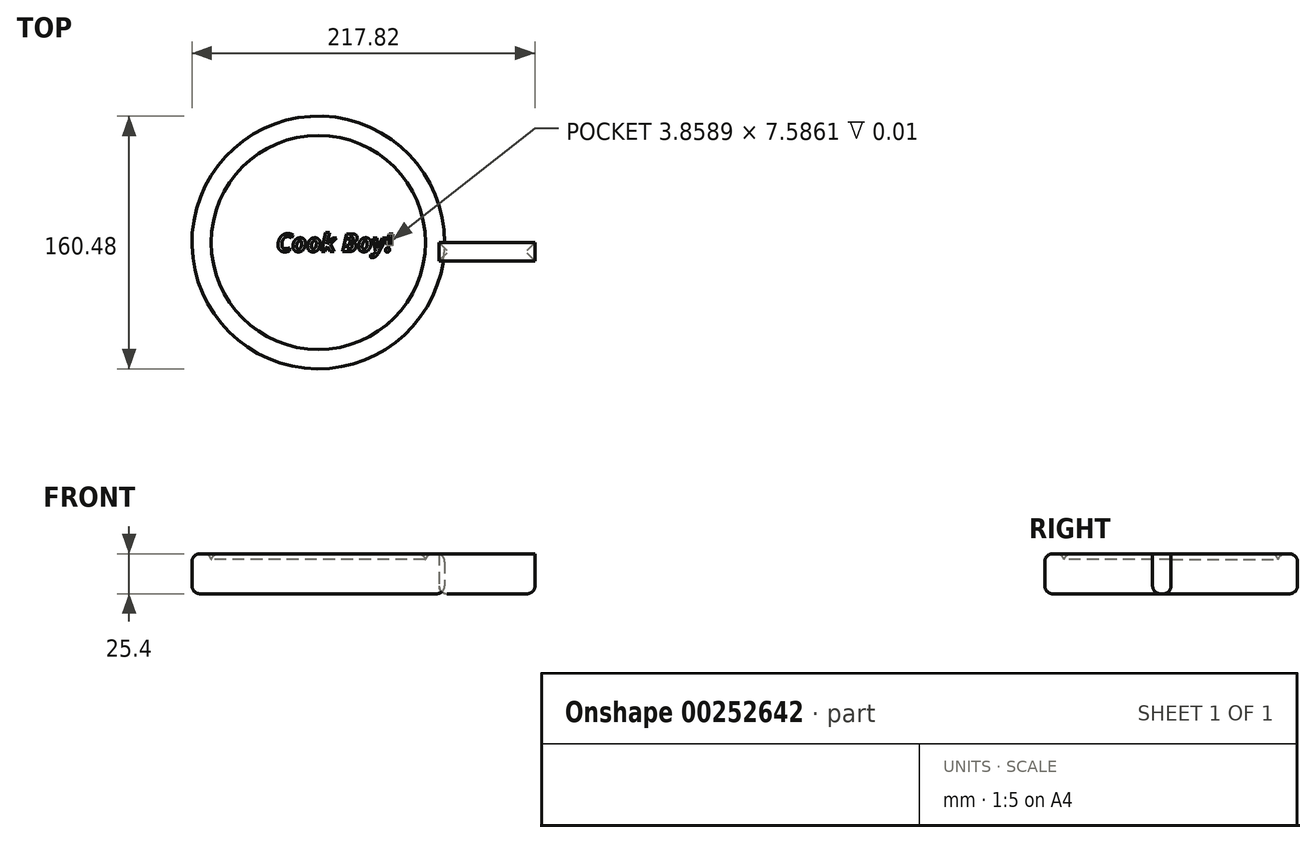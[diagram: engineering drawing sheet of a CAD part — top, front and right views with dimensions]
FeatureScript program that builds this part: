
annotation { "Feature Type Name" : "Feature", "Feature Type Description" : "" }
export const myFeature = defineFeature(function(context is Context, id is Id, definition is map)
    precondition{}
    {
        {
            var Q0;
            Q0=qCreatedBy(makeId("Top.planeOp"),FACE);
            var sketch = newSketch(context, id + "F0", { "sketchPlane" : qUnion([Q0])});
            skCircle(sketch, "E0", {"center": v(0, 0) * mm, "radius": 80.24 * mm});
            skSolve(sketch);
        }
        {
            var Q0;
            Q0=makeQuery(id+"F0.imprint","IMPRINT",FACE,{"disambiguationData":[TD([[makeQuery(id+"F0.imprint","IMPRINT",EDGE,{"derivedFrom":sQuery(id+"F0.wireOp",EDGE,"E0")}),1.0]])]});
            extrude(context, id + "F1", {"entities" : qUnion([Q0]), "depth" : 25.4 * mm});
        }
        {
            var Q0;
            Q0=makeQuery(id+"F1.opExtrude","CAP_FACE",FACE,{"disambiguationData":[OSD([sQuery(id+"F0.wireOp",EDGE,"E0")])],"isStart":false});
            var sketch = newSketch(context, id + "F2", { "sketchPlane" : qUnion([Q0])});
            skCircle(sketch, "E1", {"center": v(0, 0) * mm, "radius": 67.81 * mm});
            skSolve(sketch);
        }
        {
            var Q0;
            Q0=makeQuery(id+"F2.imprint","IMPRINT",FACE,{"disambiguationData":[TD([[makeQuery(id+"F2.imprint","IMPRINT",EDGE,{"derivedFrom":sQuery(id+"F2.wireOp",EDGE,"E1")}),1.0]])]});
            extrude(context, id + "F3", {"entities" : qUnion([Q0]), "operationType" : NewBodyOperationType.REMOVE, "oppositeDirection" : true, "depth" : 25.4 * mm});
        }
        {
            var Q0;
            Q0=makeQuery(id+"F1.opExtrude","CAP_FACE",FACE,{"disambiguationData":[OSD([sQuery(id+"F0.wireOp",EDGE,"E0")])],"isStart":false});
            fillet(context, id + "F4", {"entities" : qUnion([Q0]), "radius" : 5.08 * mm, "tangentPropagation" : true, "allowEdgeOverflow" : false});
        }
        {
            var Q0;
            Q0=qCreatedBy(makeId("Top.planeOp"),FACE);
            var sketch = newSketch(context, id + "F5", { "sketchPlane" : qUnion([Q0])});
            skCircle(sketch, "E2", {"center": v(0, 0) * mm, "radius": 68 * mm});
            skSolve(sketch);
        }
        {
            var Q0;
            Q0=makeQuery(id+"F5.imprint","IMPRINT",FACE,{"disambiguationData":[TD([[makeQuery(id+"F5.imprint","IMPRINT",EDGE,{"derivedFrom":sQuery(id+"F5.wireOp",EDGE,"E2")}),1.0]])]});
            extrude(context, id + "F6", {"entities" : qUnion([Q0]), "operationType" : NewBodyOperationType.ADD, "depth" : 25.4 * mm});
        }
        {
            var Q0;
            Q0=makeQuery(id+"F6.opExtrude","CAP_FACE",FACE,{"disambiguationData":[OSD([sQuery(id+"F5.wireOp",EDGE,"E2")])],"isStart":false});
            fillet(context, id + "F7", {"entities" : qUnion([Q0]), "radius" : 5.08 * mm, "tangentPropagation" : true, "allowEdgeOverflow" : false});
        }
        {
            var Q0;
            Q0=makeQuery(id+"F6.boolean.opBoolean","MERGE",FACE,{"derivedFrom":[makeQuery(id+"F1.opExtrude","CAP_FACE",FACE,{"disambiguationData":[OSD([sQuery(id+"F0.wireOp",EDGE,"E0")])],"isStart":true}),makeQuery(id+"F6.opExtrude","CAP_FACE",FACE,{"disambiguationData":[OSD([sQuery(id+"F5.wireOp",EDGE,"E2")])],"isStart":true})]});
            var sketch = newSketch(context, id + "F8", { "sketchPlane" : qUnion([Q0])});
            skCircle(sketch, "E3", {"center": v(0, 0) * mm, "radius": 68.22 * mm});
            skSolve(sketch);
        }
        {
            var Q0;
            Q0=makeQuery(id+"F8.imprint","IMPRINT",FACE,{"disambiguationData":[TD([[makeQuery(id+"F8.imprint","IMPRINT",EDGE,{"derivedFrom":sQuery(id+"F8.wireOp",EDGE,"E3")}),1.0]])]});
            extrude(context, id + "F9", {"entities" : qUnion([Q0]), "operationType" : NewBodyOperationType.REMOVE, "oppositeDirection" : true, "depth" : 1 / 50.8 * mm});
        }
        {
            var Q0;
            Q0=makeQuery(id+"F6.boolean.opBoolean","MERGE",FACE,{"derivedFrom":[makeQuery(id+"F1.opExtrude","CAP_FACE",FACE,{"disambiguationData":[OSD([sQuery(id+"F0.wireOp",EDGE,"E0")])],"isStart":true}),makeQuery(id+"F6.opExtrude","CAP_FACE",FACE,{"disambiguationData":[OSD([sQuery(id+"F5.wireOp",EDGE,"E2")])],"isStart":true})]});
            fillet(context, id + "F10", {"entities" : qUnion([Q0]), "radius" : 5.08 * mm, "tangentPropagation" : true, "allowEdgeOverflow" : false});
        }
        {
            var Q0;
            Q0=makeQuery(id+"F6.opExtrude","CAP_FACE",FACE,{"disambiguationData":[OSD([sQuery(id+"F5.wireOp",EDGE,"E2")])],"isStart":false});
            var sketch = newSketch(context, id + "F11", { "sketchPlane" : qUnion([Q0])});
            skText(sketch, "E4", { "text": "Cook Boy!", "fontName": "OpenSans-BoldItalic.ttf"});
            const initialGuessF11  = {"E4": [-0.02653, -0.00585, 1, 0, 0.01145]};
            skSetInitialGuess(sketch, initialGuessF11);
            skSolve(sketch);
        }
        {
            var Q0;
            Q0 = qSketchRegion(id + "F11", true);
            extrude(context, id + "F12", {"entities" : qUnion([Q0]), "operationType" : NewBodyOperationType.REMOVE, "oppositeDirection" : true, "depth" : 1 / 101.6 * mm});
        }
        {
            var Q0;
            Q0=qCreatedBy(makeId("Top.planeOp"),FACE);
            var sketch = newSketch(context, id + "F13", { "sketchPlane" : qUnion([Q0])});
            skLineSegment(sketch, "E5", {"start": v(76.52, -11.75) * mm, "end": v(137.58, -11.75) * mm});
            skLineSegment(sketch, "E6", {"start": v(137.58, -11.75) * mm, "end": v(137.58, 0) * mm});
            skLineSegment(sketch, "E7", {"start": v(137.58, 0) * mm, "end": v(76.72, 0) * mm});
            skLineSegment(sketch, "E8", {"start": v(76.72, 0) * mm, "end": v(76.52, -11.75) * mm});
            skSolve(sketch);
        }
        {
            var Q0;
            Q0 = qSketchRegion(id + "F13", true);
            extrude(context, id + "F14", {"entities" : qUnion([Q0]), "depth" : 25.4 * mm});
        }
        {
            var Q0;
            Q0=makeQuery(id+"F14.opExtrude","CAP_FACE",FACE,{"disambiguationData":[OSD([sQuery(id+"F13.wireOp",EDGE,"E5"),sQuery(id+"F13.wireOp",EDGE,"E6"),sQuery(id+"F13.wireOp",EDGE,"E7"),sQuery(id+"F13.wireOp",EDGE,"E8")])],"isStart":true});
            fillet(context, id + "F15", {"entities" : qUnion([Q0]), "radius" : 5.08 * mm, "tangentPropagation" : true, "allowEdgeOverflow" : false});
        }
    });
